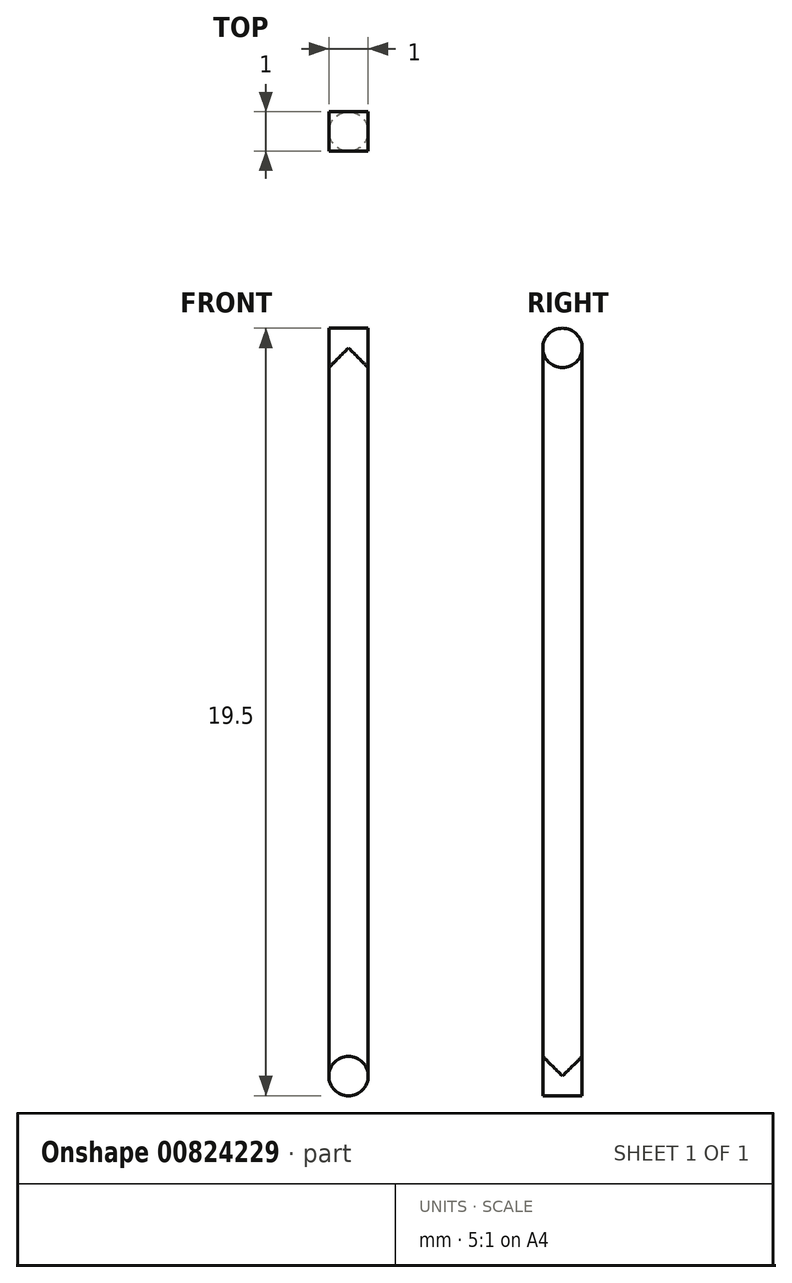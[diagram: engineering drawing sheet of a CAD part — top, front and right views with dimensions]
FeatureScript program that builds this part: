
annotation { "Feature Type Name" : "Feature", "Feature Type Description" : "" }
export const myFeature = defineFeature(function(context is Context, id is Id, definition is map)
    precondition{}
    {
        {
            var Q0;
            Q0=qCreatedBy(makeId("Top.planeOp"),FACE);
            var sketch = newSketch(context, id + "F0", { "sketchPlane" : qUnion([Q0])});
            skCircle(sketch, "E0", {"center": v(0, 0) * mm, "radius": 0.5 * mm});
            skSolve(sketch);
        }
        {
            var Q0;
            Q0 = qSketchRegion(id + "F0", true);
            extrude(context, id + "F1", {"entities" : qUnion([Q0]), "depth" : 18.5 * mm, "offsetDistance" : 25 * mm});
        }
        {
            var Q0;
            Q0=qCreatedBy(makeId("Front.planeOp"),FACE);
            var sketch = newSketch(context, id + "F2", { "sketchPlane" : qUnion([Q0])});
            skCircle(sketch, "E1", {"center": v(0, 0) * mm, "radius": 0.5 * mm});
            skSolve(sketch);
        }
        {
            var Q0;
            Q0 = qSketchRegion(id + "F2", true);
            extrude(context, id + "F3", {"entities" : qUnion([Q0]), "operationType" : NewBodyOperationType.ADD, "depth" : .5 * mm, "offsetDistance" : 25 * mm, "hasSecondDirection" : true, "secondDirectionOppositeDirection" : true, "secondDirectionDepth" : .5 * mm});
        }
        {
            var Q0;
            Q0=qCreatedBy(makeId("Right.planeOp"),FACE);
            var sketch = newSketch(context, id + "F4", { "sketchPlane" : qUnion([Q0])});
            skCircle(sketch, "E2", {"center": v(0, 18.5) * mm, "radius": 0.5 * mm});
            skSolve(sketch);
        }
        {
            var Q0;
            Q0=makeQuery(id+"F4.imprint","IMPRINT",FACE,{"disambiguationData":[TD([[makeQuery(id+"F4.imprint","IMPRINT",EDGE,{"derivedFrom":sQuery(id+"F4.wireOp",EDGE,"E2")}),1.0]])]});
            extrude(context, id + "F5", {"entities" : qUnion([Q0]), "operationType" : NewBodyOperationType.ADD, "oppositeDirection" : true, "depth" : .5 * mm, "offsetDistance" : 25 * mm, "hasSecondDirection" : true, "secondDirectionOppositeDirection" : false, "secondDirectionDepth" : .5 * mm});
        }
    });
